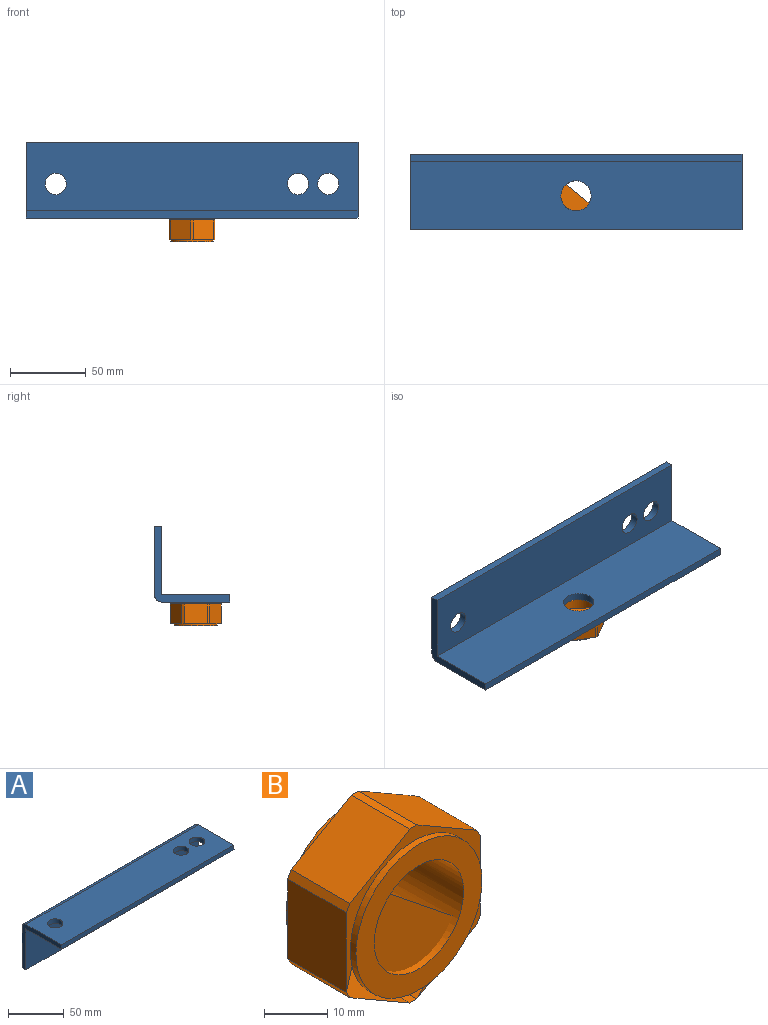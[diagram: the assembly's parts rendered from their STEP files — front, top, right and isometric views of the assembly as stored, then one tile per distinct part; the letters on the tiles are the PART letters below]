
ASSEMBLY  parts=2 mates=1
PART A: 13 faces, bbox 219.2x50x50 mm
  f0: plane 219.23x45mm, normal (0,0,-1), area 9403.9mm2, adj f1,f2,f4,f6,f10,f11,f12
  f1: plane 219.23x5mm, normal (0,-1,0), area 1096.2mm2, adj f0,f2,f4,f5
  f2: plane 50x50mm, normal (-1,0,0), area 469.6mm2, adj f0,f1,f3,f5,f6,f7,f9
  f3: plane 219.23x45mm, normal (0,1,0), area 9551.4mm2, adj f2,f4,f7,f8,f9
  f4: plane 50x50mm, normal (1,0,0), area 469.6mm2, adj f0,f1,f3,f5,f6,f7,f9
  f5: plane 219.23x45mm, normal (0,0,1), area 9403.9mm2, adj f1,f2,f4,f9,f10,f11,f12
  f6: plane 219.23x45mm, normal (0,-1,0), area 9551.4mm2, adj f0,f2,f4,f7,f8
  f7: plane 219.23x5mm, normal (0,0,-1), area 1096.2mm2, adj f2,f3,f4,f6
  f8: cylinder r=10mm len=20mm, axis (0,-1,0), area 314.1mm2, adj f3,f6
  f9: cylinder r=5mm len=219.23mm, axis (1,0,0), area 1721.8mm2, adj f2,f3,f4,f5
  f10: cylinder r=7mm len=14mm, axis (0,0,-1), area 219.9mm2, adj f0,f5
  f11: cylinder r=7mm len=14mm, axis (0,0,-1), area 219.9mm2, adj f0,f5
  f12: cylinder r=7mm len=14mm, axis (0,0,-1), area 219.9mm2, adj f0,f5
PART B: 19 faces, bbox 30x15.6x33.7 mm
  f0: cylinder r=14.08mm len=28.17mm, axis (0,-1,0), area 110.5mm2, adj f1,f2
  f1: plane 33.72x29.97mm, normal (0,1,0), area 152.4mm2, adj f0,f3,f4,f5,f6,f7,f8,f9
  f2: plane 28.55x28.17mm, normal (0,1,0), area 309.7mm2, adj f0,f15
  f3: cylinder r=16.86mm len=13.11mm, axis (0,-1,0), area 21.1mm2, adj f1,f4,f14,f16
  f4: plane 13.38x13.11mm, normal (-0.5,0,-0.87), area 202.5mm2, adj f1,f3,f5,f16
  f5: cylinder r=16.86mm len=13.11mm, axis (0,-1,0), area 21.1mm2, adj f1,f4,f6,f16
  f6: plane 15.44x13.11mm, normal (-1,0,0), area 202.5mm2, adj f1,f5,f7,f16
  f7: cylinder r=16.86mm len=13.11mm, axis (0,-1,0), area 21.1mm2, adj f1,f6,f8,f16
  f8: plane 13.38x13.11mm, normal (-0.5,0,0.87), area 202.5mm2, adj f1,f7,f9,f16
  f9: cylinder r=16.86mm len=13.11mm, axis (0,-1,0), area 21.1mm2, adj f1,f8,f10,f16
  f10: plane 13.38x13.11mm, normal (0.5,0,0.87), area 202.5mm2, adj f1,f9,f11,f16
  f11: cylinder r=16.86mm len=13.11mm, axis (0,-1,0), area 21.1mm2, adj f1,f10,f12,f16
  f12: plane 15.44x13.11mm, normal (1,0,0), area 202.5mm2, adj f1,f11,f13,f16
  f13: cylinder r=16.86mm len=13.11mm, axis (0,-1,0), area 21.1mm2, adj f1,f12,f14,f16
  f14: plane 13.38x13.11mm, normal (0.5,0,-0.87), area 202.5mm2, adj f1,f3,f13,f16
  f15: cylinder r=9.99mm len=19.98mm, axis (0,-1,0), area 979.6mm2, adj f2,f17
  f16: plane 33.72x29.97mm, normal (0,-1,0), area -159.2mm2, adj f3,f4,f5,f6,f7,f8,f9,f10
  f17: plane 28.69x28.17mm, normal (0,-1,0), area 309.7mm2, adj f15,f18
  f18: cylinder r=14.08mm len=28.17mm, axis (0,-1,0), area 110.5mm2, adj f16,f17
PLACE A rot(axis=(-1,0,0),90deg) t=(-79231.51,-8621.28,-742.36)mm
PLACE B rot(axis=(-1,0,0),90deg) t=(-79147.99,-8928.79,-782.26)mm
MATE fastened B.f3 <-> A.f8  axis (0,0,1) through (722.62,206.03,-330.48)mm
